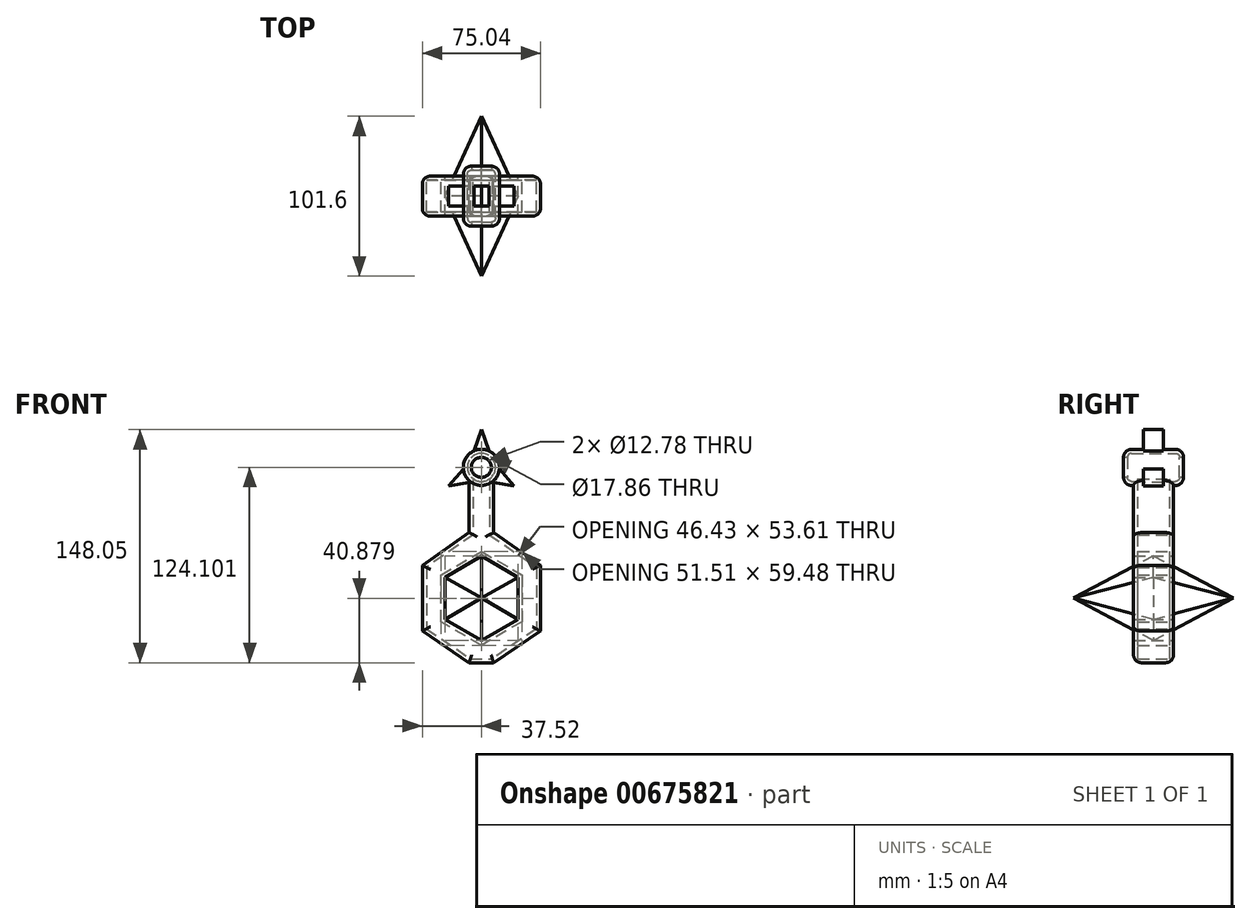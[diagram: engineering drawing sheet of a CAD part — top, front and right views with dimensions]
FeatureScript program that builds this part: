
annotation { "Feature Type Name" : "Feature", "Feature Type Description" : "" }
export const myFeature = defineFeature(function(context is Context, id is Id, definition is map)
    precondition{}
    {
        {
            var Q0;
            Q0=qCreatedBy(makeId("Front.planeOp"),FACE);
            var sketch = newSketch(context, id + "F0", { "sketchPlane" : qUnion([Q0])});
            skCircle(sketch, "E0", {"center": v(0, 51.83) * mm, "radius": 11.47 * mm});
            skLineSegment(sketch, "E1", {"start": v(-7.74, 43.36) * mm, "end": v(-7.74, 10.37) * mm});
            skLineSegment(sketch, "E2", {"start": v(-7.74, 10.37) * mm, "end": v(-37.52, -10.37) * mm});
            skLineSegment(sketch, "E3", {"start": v(-37.52, -10.37) * mm, "end": v(-37.52, -52.12) * mm});
            skLineSegment(sketch, "E4", {"start": v(-37.52, -52.12) * mm, "end": v(-7.74, -72.27) * mm});
            skLineSegment(sketch, "E5.MirrorCS", {"start": v(7.74, 43.36) * mm, "end": v(7.74, 10.37) * mm});
            skLineSegment(sketch, "E6.MirrorCS", {"start": v(7.74, 10.37) * mm, "end": v(37.52, -10.37) * mm});
            skLineSegment(sketch, "E7.MirrorCS", {"start": v(37.52, -10.37) * mm, "end": v(37.52, -52.12) * mm});
            skLineSegment(sketch, "E8.MirrorCS", {"start": v(37.52, -52.12) * mm, "end": v(7.74, -72.27) * mm});
            skLineSegment(sketch, "E9", {"start": v(-7.74, -72.27) * mm, "end": v(7.74, -72.27) * mm});
            skCircle(sketch, "E10.cCircle", {"center": v(0, -31.4) * mm, "radius": 23.21 * mm, "construction": true});
            skLineSegment(sketch, "E10.0", {"start": v(23.21, -17.99) * mm, "end": v(23.21, -44.8) * mm});
            skLineSegment(sketch, "E10.1", {"start": v(23.21, -44.8) * mm, "end": v(0, -58.2) * mm});
            skLineSegment(sketch, "E10.2", {"start": v(0, -58.2) * mm, "end": v(-23.21, -44.8) * mm});
            skLineSegment(sketch, "E10.3", {"start": v(-23.21, -44.8) * mm, "end": v(-23.21, -17.99) * mm});
            skLineSegment(sketch, "E10.4", {"start": v(-23.21, -17.99) * mm, "end": v(0, -4.58) * mm});
            skLineSegment(sketch, "E10.5", {"start": v(0, -4.58) * mm, "end": v(23.21, -17.99) * mm});
            skPoint(sketch, "E10.0.midPoint", {"position": v(23.21, -31.4) * mm});
            skLineSegment(sketch, "E11", {"start": v(-4.77, 62.27) * mm, "end": v(0, 75.78) * mm});
            skLineSegment(sketch, "E12.MirrorCS", {"start": v(4.77, 62.27) * mm, "end": v(0, 75.78) * mm});
            skSolve(sketch);
        }
        {
            var Q0;
            {var subQ1=sQuery(id+"F0.wireOp",EDGE,"E1");Q0=makeQuery(id+"F0.imprint","IMPRINT",FACE,{"disambiguationData":[TD([[makeQuery(id+"F0.imprint","IMPRINT",EDGE,{"derivedFrom":subQ1}),1.0]])]});}
            extrude(context, id + "F1", {"entities" : qUnion([Q0]), "endBound" : BoundingType.SYMMETRIC, "depth" : 25.4 * mm, "offsetDistance" : 25.4 * mm});
        }
        {
            var Q0;
            {var subQ0=sQuery(id+"F0.wireOp",EDGE,"E0");var subQ1=makeQuery(id+"F0.imprint","INTERSECT",VERTEX,{"derivedFrom":[subQ0,sQuery(id+"F0.wireOp",EDGE,"E1")]});Q0=makeQuery(id+"F0.imprint","IMPRINT",FACE,{"disambiguationData":[TD([[makeQuery(id+"F0.imprint","IMPRINT",EDGE,{"disambiguationData":[TD([[subQ1,-1.0]])],"derivedFrom":subQ0}),1.0]])]});}
            extrude(context, id + "F2", {"entities" : qUnion([Q0]), "operationType" : NewBodyOperationType.ADD, "endBound" : BoundingType.SYMMETRIC, "depth" : 38.1 * mm, "offsetDistance" : 25.4 * mm});
        }
        {
            var Q0;
            Q0=makeQuery(id+"F2.opExtrude","CAP_EDGE",EDGE,{"disambiguationData":[OSD([sQuery(id+"F0.wireOp",EDGE,"E0")])],"isStart":true});
            var Q1;
            Q1=makeQuery(id+"F2.opExtrude","CAP_EDGE",EDGE,{"disambiguationData":[OSD([sQuery(id+"F0.wireOp",EDGE,"E0")])],"isStart":false});
            fillet(context, id + "F3", {"entities" : qUnion([Q0, Q1]), "radius" : 5.08 * mm, "tangentPropagation" : true, "allowEdgeOverflow" : false});
        }
        {
            var Q0;
            Q0=makeQuery(id+"F2.opExtrude","CAP_FACE",FACE,{"disambiguationData":[OSD([sQuery(id+"F0.wireOp",EDGE,"E0")])],"isStart":true});
            var Q1;
            Q1=makeQuery(id+"F2.opExtrude","CAP_FACE",FACE,{"disambiguationData":[OSD([sQuery(id+"F0.wireOp",EDGE,"E0")])],"isStart":false});
            shell(context, id + "F4", {"entities" : qUnion([Q0, Q1]), "thickness" : 2.54 * mm});
        }
        {
            var Q0;
            Q0=makeQuery(id+"F1.opExtrude","CAP_EDGE",EDGE,{"disambiguationData":[OSD([sQuery(id+"F0.wireOp",EDGE,"E1")])],"isStart":false});
            var Q1;
            Q1=makeQuery(id+"F1.opExtrude","CAP_EDGE",EDGE,{"disambiguationData":[OSD([sQuery(id+"F0.wireOp",EDGE,"E1")])],"isStart":true});
            var Q2;
            Q2=makeQuery(id+"F1.opExtrude","CAP_EDGE",EDGE,{"disambiguationData":[OSD([sQuery(id+"F0.wireOp",EDGE,"E5.MirrorCS")])],"isStart":true});
            var Q3;
            Q3=makeQuery(id+"F1.opExtrude","CAP_EDGE",EDGE,{"disambiguationData":[OSD([sQuery(id+"F0.wireOp",EDGE,"E5.MirrorCS")])],"isStart":false});
            fillet(context, id + "F5", {"entities" : qUnion([Q0, Q1, Q2, Q3]), "radius" : 5.08 * mm, "tangentPropagation" : true, "allowEdgeOverflow" : false});
        }
        {
            var Q0;
            Q0=makeQuery(id+"F1.opExtrude","CAP_EDGE",EDGE,{"disambiguationData":[OSD([sQuery(id+"F0.wireOp",EDGE,"E7.MirrorCS")])],"isStart":false});
            var Q1;
            Q1=makeQuery(id+"F1.opExtrude","CAP_EDGE",EDGE,{"disambiguationData":[OSD([sQuery(id+"F0.wireOp",EDGE,"E7.MirrorCS")])],"isStart":true});
            var Q2;
            Q2=makeQuery(id+"F1.opExtrude","CAP_EDGE",EDGE,{"disambiguationData":[OSD([sQuery(id+"F0.wireOp",EDGE,"E6.MirrorCS")])],"isStart":true});
            var Q3;
            Q3=makeQuery(id+"F1.opExtrude","CAP_EDGE",EDGE,{"disambiguationData":[OSD([sQuery(id+"F0.wireOp",EDGE,"E6.MirrorCS")])],"isStart":false});
            var Q4;
            Q4=makeQuery(id+"F1.opExtrude","CAP_EDGE",EDGE,{"disambiguationData":[OSD([sQuery(id+"F0.wireOp",EDGE,"E8.MirrorCS")])],"isStart":true});
            var Q5;
            Q5=makeQuery(id+"F1.opExtrude","CAP_EDGE",EDGE,{"disambiguationData":[OSD([sQuery(id+"F0.wireOp",EDGE,"E8.MirrorCS")])],"isStart":false});
            var Q6;
            Q6=makeQuery(id+"F1.opExtrude","CAP_EDGE",EDGE,{"disambiguationData":[OSD([sQuery(id+"F0.wireOp",EDGE,"E9")])],"isStart":true});
            var Q7;
            Q7=makeQuery(id+"F1.opExtrude","CAP_EDGE",EDGE,{"disambiguationData":[OSD([sQuery(id+"F0.wireOp",EDGE,"E9")])],"isStart":false});
            var Q8;
            Q8=makeQuery(id+"F1.opExtrude","CAP_EDGE",EDGE,{"disambiguationData":[OSD([sQuery(id+"F0.wireOp",EDGE,"E4")])],"isStart":true});
            var Q9;
            Q9=makeQuery(id+"F1.opExtrude","CAP_EDGE",EDGE,{"disambiguationData":[OSD([sQuery(id+"F0.wireOp",EDGE,"E4")])],"isStart":false});
            var Q10;
            Q10=makeQuery(id+"F1.opExtrude","CAP_EDGE",EDGE,{"disambiguationData":[OSD([sQuery(id+"F0.wireOp",EDGE,"E3")])],"isStart":false});
            var Q11;
            Q11=makeQuery(id+"F1.opExtrude","CAP_EDGE",EDGE,{"disambiguationData":[OSD([sQuery(id+"F0.wireOp",EDGE,"E3")])],"isStart":true});
            var Q12;
            Q12=makeQuery(id+"F1.opExtrude","CAP_EDGE",EDGE,{"disambiguationData":[OSD([sQuery(id+"F0.wireOp",EDGE,"E2")])],"isStart":true});
            var Q13;
            Q13=makeQuery(id+"F1.opExtrude","CAP_EDGE",EDGE,{"disambiguationData":[OSD([sQuery(id+"F0.wireOp",EDGE,"E2")])],"isStart":false});
            fillet(context, id + "F6", {"entities" : qUnion([Q0, Q1, Q2, Q3, Q4, Q5, Q6, Q7, Q8, Q9, Q10, Q11, Q12, Q13]), "radius" : 5.08 * mm, "tangentPropagation" : true, "defaultsChanged" : false, "vertexSettings" : [], "allowEdgeOverflow" : false});
        }
        {
            var Q0;
            Q0=qCreatedBy(makeId("Front.planeOp"),FACE);
            cPlane(context, id + "F7", {"entities" : qUnion([Q0]), "cplaneType" : CPlaneType.OFFSET, "offset" : 50.8 * mm, "width" : 152.4 * mm, "height" : 152.4 * mm});
        }
        {
            var Q0;
            Q0=qCreatedBy(id+"F7.planeOp",FACE);
            var sketch = newSketch(context, id + "F8", { "sketchPlane" : qUnion([Q0])});
            skPoint(sketch, "E13", {"position": v(0, -31.1) * mm});
            skSolve(sketch);
        }
        {
            var Q0;
            Q0=makeQuery(id+"F0.imprint","IMPRINT",FACE,{"disambiguationData":[TD([[makeQuery(id+"F0.imprint","IMPRINT",EDGE,{"derivedFrom":sQuery(id+"F0.wireOp",EDGE,"E10.0")}),-1.0]])]});
            var Q1;
            Q1=sQuery(id+"F8.wireOp",VERTEX,"E13");
            var Q2;
            Q2=sQuery(id+"F0.wireOp",VERTEX,"E10.3.end");
            var Q3;
            Q3=sQuery(id+"F0.wireOp",VERTEX,"E10.4.end");
            var Q4;
            Q4=sQuery(id+"F0.wireOp",VERTEX,"E10.0.start");
            var Q5;
            Q5=sQuery(id+"F0.wireOp",VERTEX,"E10.0.end");
            var Q6;
            Q6=sQuery(id+"F0.wireOp",VERTEX,"E10.1.end");
            var Q7;
            Q7=sQuery(id+"F0.wireOp",VERTEX,"E10.2.end");
            loft(context, id + "F9", {"operationType" : NewBodyOperationType.ADD, "sheetProfilesArray" : [{ "sheetProfileEntities" : qUnion([Q0]) }, { "sheetProfileEntities" : qUnion([Q1]) }], "connections" : [{ "connectionEntities" : qUnion([Q2, Q3, Q4, Q5, Q6, Q7]), "connectionEdgeQueries" : qUnion([]), "connectionEdgeParameters" : [] }]});
        }
        {
            var Q0;
            Q0=makeQuery(id+"F9.opLoft","SWEPT_BODY",BODY,{"disambiguationData":[OSD([makeQuery(id+"F0.imprint","IMPRINT",FACE,{"disambiguationData":[TD([[makeQuery(id+"F0.imprint","IMPRINT",EDGE,{"derivedFrom":sQuery(id+"F0.wireOp",EDGE,"E10.0")}),-1.0]])]}),sQuery(id+"F8.wireOp",VERTEX,"E13")])]});
            var Q1;
            Q1=qCreatedBy(makeId("Front.planeOp"),FACE);
            mirror(context, id + "F10", {"operationType" : NewBodyOperationType.ADD, "entities" : qUnion([Q0]), "mirrorPlane" : qUnion([Q1])});
        }
        {
            var Q0;
            {var subQ0=sQuery(id+"F0.wireOp",EDGE,"E11");Q0=makeQuery(id+"F0.imprint","IMPRINT",FACE,{"disambiguationData":[TD([[makeQuery(id+"F0.imprint","IMPRINT",EDGE,{"derivedFrom":subQ0}),-1.0]])]});}
            extrude(context, id + "F11", {"entities" : qUnion([Q0]), "endBound" : BoundingType.SYMMETRIC, "depth" : 12.7 * mm, "offsetDistance" : 25.4 * mm});
        }
        {
            var Q0;
            Q0=makeQuery(id+"F11.opExtrude","SWEPT_BODY",BODY,{"disambiguationData":[OSD([sQuery(id+"F0.wireOp",EDGE,"E0"),sQuery(id+"F0.wireOp",EDGE,"E11"),sQuery(id+"F0.wireOp",EDGE,"E12.MirrorCS")])]});
            var Q1;
            Q1=sQuery(id+"F0.wireOp",EDGE,"E0");
            circularPattern(context, id + "F12", {"operationType" : NewBodyOperationType.ADD, "entities" : qUnion([Q0]), "axis" : qUnion([Q1]), "angle" : 360 * degree, "instanceCount" : 3, "equalSpace" : true});
        }
    });
